# Revit family: AudienceSystems_RetractableSeating_Espace628_EndAisles
name_source: partatom
category: Furniture
revit_build: Autodesk Revit 2015 (Build: 20160220_1515(x64)
units: mm (PartAtom-declared; Revit-internal decimal feet)

## types (1)
- AudienceSystems_RetractableSeating_Espace628_EndAisles
    Assembly Code = E2020400
    AssetType = Movable
    BIMObjectName = BIMBox_AudienceSystems_RetractableSeating_Espace628EndAisles
    Category = Pr_40_30_29_72: Retractable Seats
    CodePerformance = Strength: certified to BS EN 12727:2000; Flammability: Upholstery fabric/foam comply with BS 5852 1990
    Color = <Primary Colour of Product>
    Constituents = Espace 628 Chair, Retractable Seating, End Aisles
    Cost = 0 $
    Description = TX is operationally durable enough for the largest arena installation but refined enough for education, arts and conference facility operators.
    DurationUnit = Year
    ExpectedLife = 10
    Features = Self Tipping Design; Compact dimensions when closed; For use on min 280mm row rise/ 800mm row depth telescopic platforms; Wide range of options and enhancements
    Finish = Fabric Seat & Back; ABS Arm
    HighestSeatingHeight = 455 mm
    IfcExportAs = IfcFurnishingElementType
    IfcExportType = UNDEFINED
    Keynote = Pr_40_30_29_72
    LowestSeatingHeight = 445 mm  [stored 1.45997 ft]
    MainColor = <Primary Colour of Product>
    ManufacturerAddressUK = 19B Washington Road, West Wilts Trading Estate , Westbury, Wiltshire, BA13 4JP
    ManufacturerName = Audience Systems Ltd
    ManufacturerURL = http://www.audiencesystems.com
    Material = Seat: Polyurethane CMHR / CME foam, Backrest: Polyurethane CMHR / CME foam, Arm: ABS Injection Moulding
    Model = Espace628onTXPlatform
    ModelNumber = Espace628onTXPlatform
    ModelReference = Espace628onTXPlatformwithEndAisles
    NBSDescription = Auditoria fittings, furnishings and equipment system
    NBSReference = 35-15-05/105
    Name = RetractableSeating_Espace628withEndAisles_AudienceSystems
    ProductInformation = http://www.audiencesystems.com
    Shape = Various
    Size = Please refer to Nominal Dimensions for overall size of Auditorium Seating
    Style = Auditorium Seating
    URL = http://www.audiencesystems.com
    Uniclass2015Description = Retractable Seats
    Uniclass2015Reference = Pr_40_30_29_72
    Uniclass2015Version = Products v1.1
    Version = 1
    WarrantyDurationLabor = 10
    WarrantyDurationParts = 10
    WarrantyDurationUnit = Year

note: [stored X ft] marks values corroborated as IEEE doubles in the binary element streams (Revit-internal decimal feet)

## geometry (parser evidence)
native form markers: Sweep x25
no freeform markers — native parametric forms only
